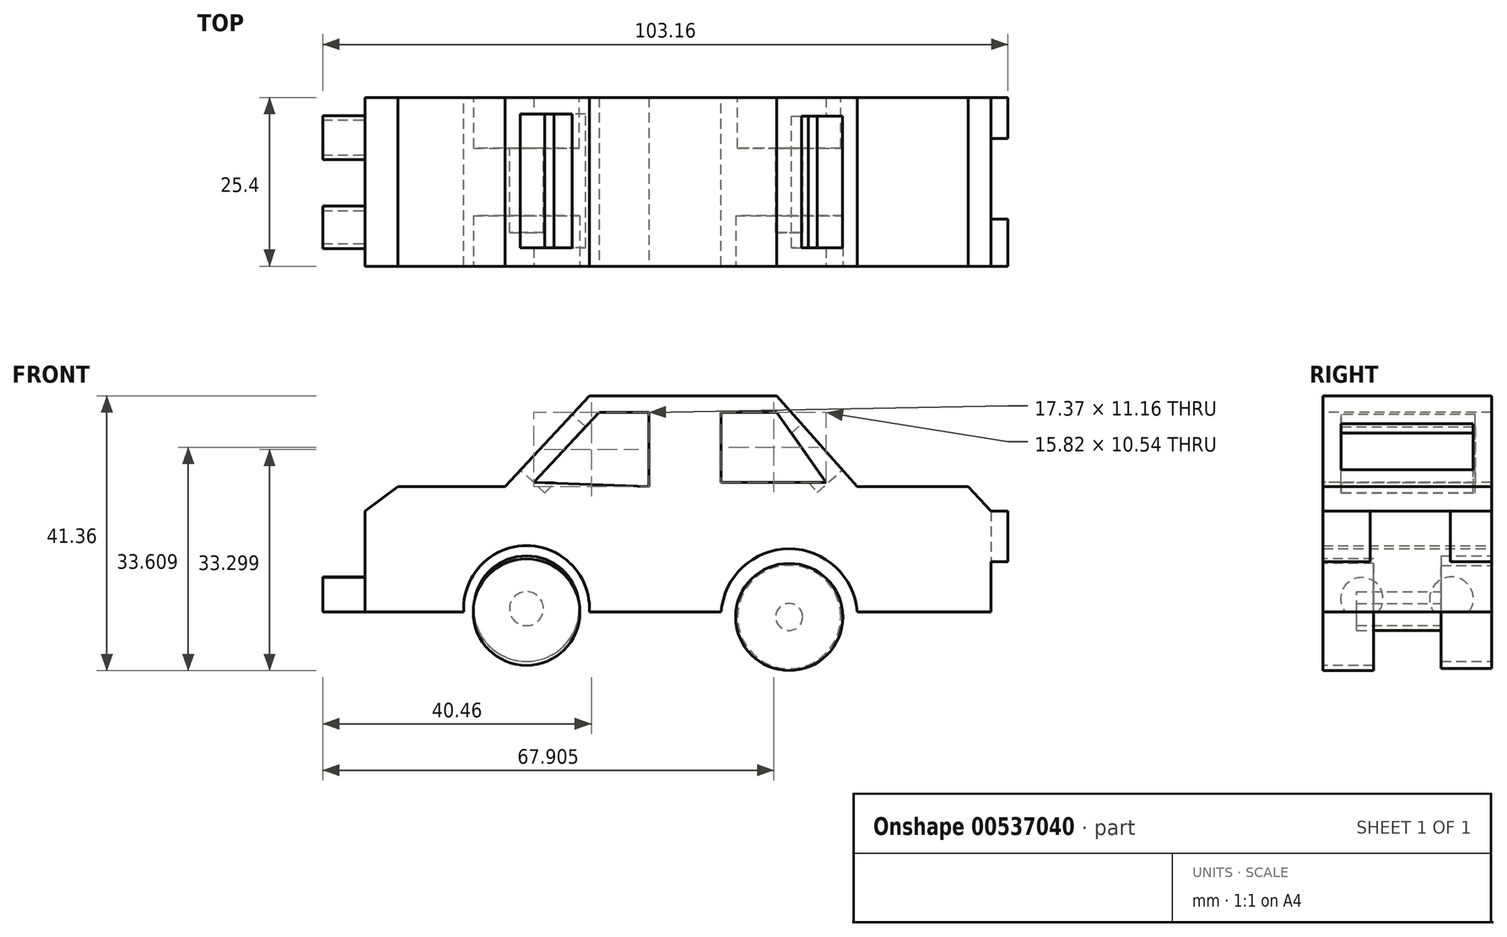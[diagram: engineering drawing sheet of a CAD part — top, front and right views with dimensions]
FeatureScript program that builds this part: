
annotation { "Feature Type Name" : "Feature", "Feature Type Description" : "" }
export const myFeature = defineFeature(function(context is Context, id is Id, definition is map)
    precondition{}
    {
        {
            var Q0;
            Q0=qCreatedBy(makeId("Front.planeOp"),FACE);
            var sketch = newSketch(context, id + "F0", { "sketchPlane" : qUnion([Q0])});
            skLineSegment(sketch, "E0", {"start": v(0, 0) * mm, "end": v(19.85, 0) * mm});
            skArc(sketch, "E1", {"start": v(40.32, 0) * mm, "mid": v(30.08, 9.53) * mm, "end": v(19.85, 0) * mm});
            skArc(sketch, "E2", {"start": v(0, 0) * mm, "mid": v(-9.46, 10) * mm, "end": v(-18.92, 0) * mm});
            skLineSegment(sketch, "E3", {"start": v(-18.92, 0) * mm, "end": v(-33.8, 0) * mm});
            skLineSegment(sketch, "E4", {"start": v(-33.8, 0) * mm, "end": v(-33.8, 15.2) * mm});
            skLineSegment(sketch, "E5", {"start": v(-33.8, 15.2) * mm, "end": v(-28.84, 18.92) * mm});
            skLineSegment(sketch, "E6", {"start": v(-28.84, 18.92) * mm, "end": v(-12.71, 18.92) * mm});
            skLineSegment(sketch, "E7", {"start": v(-12.71, 18.92) * mm, "end": v(0, 32.56) * mm});
            skLineSegment(sketch, "E8", {"start": v(0, 32.56) * mm, "end": v(28.22, 32.56) * mm});
            skLineSegment(sketch, "E9", {"start": v(28.22, 32.56) * mm, "end": v(40.32, 18.92) * mm});
            skLineSegment(sketch, "E10", {"start": v(40.32, 18.92) * mm, "end": v(57.06, 18.92) * mm});
            skLineSegment(sketch, "E11", {"start": v(57.06, 18.92) * mm, "end": v(60.47, 15.2) * mm});
            skLineSegment(sketch, "E12", {"start": v(60.47, 15.2) * mm, "end": v(60.47, 0) * mm});
            skLineSegment(sketch, "E13", {"start": v(60.47, 0) * mm, "end": v(40.32, 0) * mm});
            skSolve(sketch);
        }
        {
            var Q0;
            Q0=makeQuery(id+"F0.imprint","IMPRINT",FACE,{"disambiguationData":[TD([[makeQuery(id+"F0.imprint","IMPRINT",EDGE,{"derivedFrom":sQuery(id+"F0.wireOp",EDGE,"E0")}),1.0]])]});
            extrude(context, id + "F1", {"entities" : qUnion([Q0]), "depth" : 25.4 * mm, "offsetDistance" : 25.4 * mm});
        }
        {
            var Q0;
            Q0=makeQuery(id+"F1.opExtrude","CAP_FACE",FACE,{"disambiguationData":[OSD([sQuery(id+"F0.wireOp",EDGE,"E0"),sQuery(id+"F0.wireOp",EDGE,"E1"),sQuery(id+"F0.wireOp",EDGE,"E2"),sQuery(id+"F0.wireOp",EDGE,"E3"),sQuery(id+"F0.wireOp",EDGE,"E4"),sQuery(id+"F0.wireOp",EDGE,"E5"),sQuery(id+"F0.wireOp",EDGE,"E6"),sQuery(id+"F0.wireOp",EDGE,"E7"),sQuery(id+"F0.wireOp",EDGE,"E8"),sQuery(id+"F0.wireOp",EDGE,"E9"),sQuery(id+"F0.wireOp",EDGE,"E10"),sQuery(id+"F0.wireOp",EDGE,"E11"),sQuery(id+"F0.wireOp",EDGE,"E12"),sQuery(id+"F0.wireOp",EDGE,"E13")])],"isStart":false});
            var sketch = newSketch(context, id + "F2", { "sketchPlane" : qUnion([Q0])});
            skCircle(sketch, "E14", {"center": v(-9.46, 0) * mm, "radius": 8.02 * mm});
            skPoint(sketch, "E14.centerSnap0", {"position": v(-9.46, 10) * mm});
            skCircle(sketch, "E15", {"center": v(30.08, -0.73) * mm, "radius": 8.07 * mm});
            skSolve(sketch);
        }
        {
            var Q0;
            Q0=makeQuery(id+"F2.imprint","IMPRINT",FACE,{"disambiguationData":[TD([[makeQuery(id+"F2.imprint","IMPRINT",EDGE,{"derivedFrom":sQuery(id+"F2.wireOp",EDGE,"E14")}),1.0]])]});
            var Q1;
            Q1=makeQuery(id+"F2.imprint","IMPRINT",FACE,{"disambiguationData":[TD([[makeQuery(id+"F2.imprint","IMPRINT",EDGE,{"derivedFrom":sQuery(id+"F2.wireOp",EDGE,"E15")}),1.0]])]});
            extrude(context, id + "F3", {"entities" : qUnion([Q0, Q1]), "oppositeDirection" : true, "depth" : 7.62 * mm, "offsetDistance" : 25.4 * mm});
        }
        {
            var Q0;
            Q0=makeQuery(id+"F1.opExtrude","CAP_FACE",FACE,{"disambiguationData":[OSD([sQuery(id+"F0.wireOp",EDGE,"E0"),sQuery(id+"F0.wireOp",EDGE,"E1"),sQuery(id+"F0.wireOp",EDGE,"E2"),sQuery(id+"F0.wireOp",EDGE,"E3"),sQuery(id+"F0.wireOp",EDGE,"E4"),sQuery(id+"F0.wireOp",EDGE,"E5"),sQuery(id+"F0.wireOp",EDGE,"E6"),sQuery(id+"F0.wireOp",EDGE,"E7"),sQuery(id+"F0.wireOp",EDGE,"E8"),sQuery(id+"F0.wireOp",EDGE,"E9"),sQuery(id+"F0.wireOp",EDGE,"E10"),sQuery(id+"F0.wireOp",EDGE,"E11"),sQuery(id+"F0.wireOp",EDGE,"E12"),sQuery(id+"F0.wireOp",EDGE,"E13")])],"isStart":true});
            var sketch = newSketch(context, id + "F4", { "sketchPlane" : qUnion([Q0])});
            skCircle(sketch, "E16", {"center": v(-30.08, -0.73) * mm, "radius": 7.77 * mm});
            skCircle(sketch, "E17", {"center": v(9.46, 0.53) * mm, "radius": 7.94 * mm});
            skSolve(sketch);
        }
        {
            var Q0;
            Q0=makeQuery(id+"F4.imprint","IMPRINT",FACE,{"disambiguationData":[TD([[makeQuery(id+"F4.imprint","IMPRINT",EDGE,{"derivedFrom":sQuery(id+"F4.wireOp",EDGE,"E16")}),1.0]])]});
            var Q1;
            Q1=makeQuery(id+"F4.imprint","IMPRINT",FACE,{"disambiguationData":[TD([[makeQuery(id+"F4.imprint","IMPRINT",EDGE,{"derivedFrom":sQuery(id+"F4.wireOp",EDGE,"E17")}),1.0]])]});
            extrude(context, id + "F5", {"entities" : qUnion([Q0, Q1]), "oppositeDirection" : true, "depth" : 7.62 * mm, "offsetDistance" : 25.4 * mm});
        }
        {
            var Q0;
            Q0=makeQuery(id+"F5.opExtrude","CAP_FACE",FACE,{"disambiguationData":[OSD([sQuery(id+"F4.wireOp",EDGE,"E16")])],"isStart":false});
            var sketch = newSketch(context, id + "F6", { "sketchPlane" : qUnion([Q0])});
            skCircle(sketch, "E18", {"center": v(30.08, -0.73) * mm, "radius": 2.03 * mm});
            skSolve(sketch);
        }
        {
            var Q0;
            Q0=makeQuery(id+"F6.imprint","IMPRINT",FACE,{"disambiguationData":[TD([[makeQuery(id+"F6.imprint","IMPRINT",EDGE,{"derivedFrom":sQuery(id+"F6.wireOp",EDGE,"E18")}),1.0]])]});
            extrude(context, id + "F7", {"entities" : qUnion([Q0]), "depth" : 12.7 * mm, "offsetDistance" : 25.4 * mm});
        }
        {
            var Q0;
            Q0=makeQuery(id+"F5.opExtrude","CAP_FACE",FACE,{"disambiguationData":[OSD([sQuery(id+"F4.wireOp",EDGE,"E17")])],"isStart":false});
            var sketch = newSketch(context, id + "F8", { "sketchPlane" : qUnion([Q0])});
            skCircle(sketch, "E19", {"center": v(-9.46, 0.53) * mm, "radius": 2.55 * mm});
            skSolve(sketch);
        }
        {
            var Q0;
            Q0=makeQuery(id+"F8.imprint","IMPRINT",FACE,{"disambiguationData":[TD([[makeQuery(id+"F8.imprint","IMPRINT",EDGE,{"derivedFrom":sQuery(id+"F8.wireOp",EDGE,"E19")}),1.0]])]});
            extrude(context, id + "F9", {"entities" : qUnion([Q0]), "depth" : 12.7 * mm, "offsetDistance" : 25.4 * mm});
        }
        {
            var Q0;
            Q0=makeQuery(id+"F1.opExtrude","SWEPT_FACE",FACE,{"disambiguationData":[OSD([sQuery(id+"F0.wireOp",EDGE,"E12")])]});
            var sketch = newSketch(context, id + "F10", { "sketchPlane" : qUnion([Q0])});
            skLineSegment(sketch, "E20", {"start": v(-18.3, 15.2) * mm, "end": v(-18.3, 7.6) * mm});
            skPoint(sketch, "E20.endSnap0", {"position": v(-25.4, 7.6) * mm});
            skLineSegment(sketch, "E21", {"start": v(-18.3, 7.6) * mm, "end": v(-25.4, 7.6) * mm});
            skLineSegment(sketch, "E22", {"start": v(-25.4, 7.6) * mm, "end": v(-25.4, 15.2) * mm});
            skLineSegment(sketch, "E23", {"start": v(-25.4, 15.2) * mm, "end": v(-18.3, 15.2) * mm});
            skLineSegment(sketch, "E24", {"start": v(0, 15.2) * mm, "end": v(-6.2, 15.2) * mm});
            skLineSegment(sketch, "E25", {"start": v(-6.2, 15.2) * mm, "end": v(-6.2, 7.6) * mm});
            skLineSegment(sketch, "E26", {"start": v(-6.2, 7.6) * mm, "end": v(0, 7.6) * mm});
            skLineSegment(sketch, "E27", {"start": v(0, 7.6) * mm, "end": v(0, 15.2) * mm});
            skSolve(sketch);
        }
        {
            var Q0;
            Q0=makeQuery(id+"F10.imprint","IMPRINT",FACE,{"disambiguationData":[TD([[makeQuery(id+"F10.imprint","IMPRINT",EDGE,{"derivedFrom":sQuery(id+"F10.wireOp",EDGE,"E24")}),-1.0]])]});
            var Q1;
            Q1=makeQuery(id+"F10.imprint","IMPRINT",FACE,{"disambiguationData":[TD([[makeQuery(id+"F10.imprint","IMPRINT",EDGE,{"derivedFrom":sQuery(id+"F10.wireOp",EDGE,"E20")}),-1.0]])]});
            extrude(context, id + "F11", {"entities" : qUnion([Q0, Q1]), "operationType" : NewBodyOperationType.ADD, "depth" : 2.54 * mm, "offsetDistance" : 25.4 * mm});
        }
        {
            var Q0;
            Q0=makeQuery(id+"F11.boolean.opBoolean","MERGE",FACE,{"derivedFrom":[makeQuery(id+"F1.opExtrude","CAP_FACE",FACE,{"disambiguationData":[OSD([sQuery(id+"F0.wireOp",EDGE,"E0"),sQuery(id+"F0.wireOp",EDGE,"E1"),sQuery(id+"F0.wireOp",EDGE,"E2"),sQuery(id+"F0.wireOp",EDGE,"E3"),sQuery(id+"F0.wireOp",EDGE,"E4"),sQuery(id+"F0.wireOp",EDGE,"E5"),sQuery(id+"F0.wireOp",EDGE,"E6"),sQuery(id+"F0.wireOp",EDGE,"E7"),sQuery(id+"F0.wireOp",EDGE,"E8"),sQuery(id+"F0.wireOp",EDGE,"E9"),sQuery(id+"F0.wireOp",EDGE,"E10"),sQuery(id+"F0.wireOp",EDGE,"E11"),sQuery(id+"F0.wireOp",EDGE,"E12"),sQuery(id+"F0.wireOp",EDGE,"E13")])],"isStart":false}),makeQuery(id+"F11.opExtrude","SWEPT_FACE",FACE,{"disambiguationData":[OSD([sQuery(id+"F10.wireOp",EDGE,"E22")])]})]});
            var sketch = newSketch(context, id + "F12", { "sketchPlane" : qUnion([Q0])});
            skLineSegment(sketch, "E28", {"start": v(35.66, 19.54) * mm, "end": v(19.85, 19.54) * mm});
            skLineSegment(sketch, "E29", {"start": v(19.85, 19.54) * mm, "end": v(19.85, 30.08) * mm});
            skLineSegment(sketch, "E30", {"start": v(19.85, 30.08) * mm, "end": v(28.22, 30.08) * mm});
            skLineSegment(sketch, "E31", {"start": v(28.22, 30.08) * mm, "end": v(35.66, 19.54) * mm});
            skLineSegment(sketch, "E32", {"start": v(-8.37, 19.54) * mm, "end": v(1.45, 30.08) * mm});
            skLineSegment(sketch, "E33", {"start": v(1.45, 30.08) * mm, "end": v(9, 30.08) * mm});
            skLineSegment(sketch, "E34", {"start": v(9, 30.08) * mm, "end": v(9, 18.92) * mm});
            skLineSegment(sketch, "E35", {"start": v(9, 18.92) * mm, "end": v(-8.37, 19.54) * mm});
            skSolve(sketch);
        }
        {
            var Q0;
            Q0=makeQuery(id+"F12.imprint","IMPRINT",FACE,{"disambiguationData":[TD([[makeQuery(id+"F12.imprint","IMPRINT",EDGE,{"derivedFrom":sQuery(id+"F12.wireOp",EDGE,"E28")}),-1.0]])]});
            var Q1;
            Q1=makeQuery(id+"F12.imprint","IMPRINT",FACE,{"disambiguationData":[TD([[makeQuery(id+"F12.imprint","IMPRINT",EDGE,{"derivedFrom":sQuery(id+"F12.wireOp",EDGE,"E32")}),-1.0]])]});
            extrude(context, id + "F13", {"entities" : qUnion([Q0, Q1]), "operationType" : NewBodyOperationType.REMOVE, "oppositeDirection" : true, "depth" : 25.4 * mm, "offsetDistance" : 25.4 * mm});
        }
        {
            var Q0;
            Q0=makeQuery(id+"F1.opExtrude","SWEPT_FACE",FACE,{"disambiguationData":[OSD([sQuery(id+"F0.wireOp",EDGE,"E9")])]});
            var sketch = newSketch(context, id + "F14", { "sketchPlane" : qUnion([Q0])});
            skLineSegment(sketch, "E36", {"start": v(-22.64, 0) * mm, "end": v(-22.64, -9.27) * mm});
            skLineSegment(sketch, "E37", {"start": v(-22.64, -9.27) * mm, "end": v(-2.8, -9.27) * mm});
            skLineSegment(sketch, "E38", {"start": v(-2.8, -9.27) * mm, "end": v(-2.8, 0) * mm});
            skLineSegment(sketch, "E39", {"start": v(-2.8, 0) * mm, "end": v(-22.64, 0) * mm});
            skSolve(sketch);
        }
        {
            var Q0;
            Q0=makeQuery(id+"F14.imprint","IMPRINT",FACE,{"disambiguationData":[TD([[makeQuery(id+"F14.imprint","IMPRINT",EDGE,{"derivedFrom":sQuery(id+"F14.wireOp",EDGE,"E36")}),1.0]])]});
            extrude(context, id + "F15", {"entities" : qUnion([Q0]), "operationType" : NewBodyOperationType.REMOVE, "oppositeDirection" : true, "depth" : 5.08 * mm, "offsetDistance" : 25.4 * mm});
        }
        {
            var Q0;
            Q0=makeQuery(id+"F1.opExtrude","SWEPT_FACE",FACE,{"disambiguationData":[OSD([sQuery(id+"F0.wireOp",EDGE,"E7")])]});
            var sketch = newSketch(context, id + "F16", { "sketchPlane" : qUnion([Q0])});
            skLineSegment(sketch, "E40", {"start": v(2.48, 20) * mm, "end": v(22.64, 20) * mm});
            skLineSegment(sketch, "E41", {"start": v(22.64, 20) * mm, "end": v(22.64, 8.56) * mm});
            skLineSegment(sketch, "E42", {"start": v(22.64, 8.56) * mm, "end": v(2.48, 8.56) * mm});
            skLineSegment(sketch, "E43", {"start": v(2.48, 8.56) * mm, "end": v(2.48, 20) * mm});
            skSolve(sketch);
        }
        {
            var Q0;
            Q0=makeQuery(id+"F16.imprint","IMPRINT",FACE,{"disambiguationData":[TD([[makeQuery(id+"F16.imprint","IMPRINT",EDGE,{"derivedFrom":sQuery(id+"F16.wireOp",EDGE,"E40")}),-1.0]])]});
            extrude(context, id + "F17", {"entities" : qUnion([Q0]), "operationType" : NewBodyOperationType.REMOVE, "oppositeDirection" : true, "depth" : 5.08 * mm, "offsetDistance" : 25.4 * mm});
        }
        {
            var Q0;
            Q0=makeQuery(id+"F1.opExtrude","SWEPT_FACE",FACE,{"disambiguationData":[OSD([sQuery(id+"F0.wireOp",EDGE,"E4")])]});
            var sketch = newSketch(context, id + "F18", { "sketchPlane" : qUnion([Q0])});
            skArc(sketch, "E44", {"start": v(8.68, 0) * mm, "mid": v(6.05, 5.3) * mm, "end": v(3.41, 0) * mm});
            skArc(sketch, "E45", {"start": v(22.02, 0) * mm, "mid": v(19.54, 5.21) * mm, "end": v(17.06, 0) * mm});
            skSolve(sketch);
        }
        {
            var Q0;
            {var subQ0=sQuery(id+"F18.wireOp",EDGE,"E45");Q0=makeQuery(id+"F18.imprint","IMPRINT",FACE,{"disambiguationData":[TD([[makeQuery(id+"F18.imprint","IMPRINT",EDGE,{"derivedFrom":subQ0}),1.0]])]});}
            var Q1;
            {var subQ0=sQuery(id+"F18.wireOp",EDGE,"E44");Q1=makeQuery(id+"F18.imprint","IMPRINT",FACE,{"disambiguationData":[TD([[makeQuery(id+"F18.imprint","IMPRINT",EDGE,{"derivedFrom":subQ0}),1.0]])]});}
            extrude(context, id + "F19", {"entities" : qUnion([Q0, Q1]), "operationType" : NewBodyOperationType.ADD, "depth" : 6.35 * mm, "offsetDistance" : 25.4 * mm});
        }
    });
